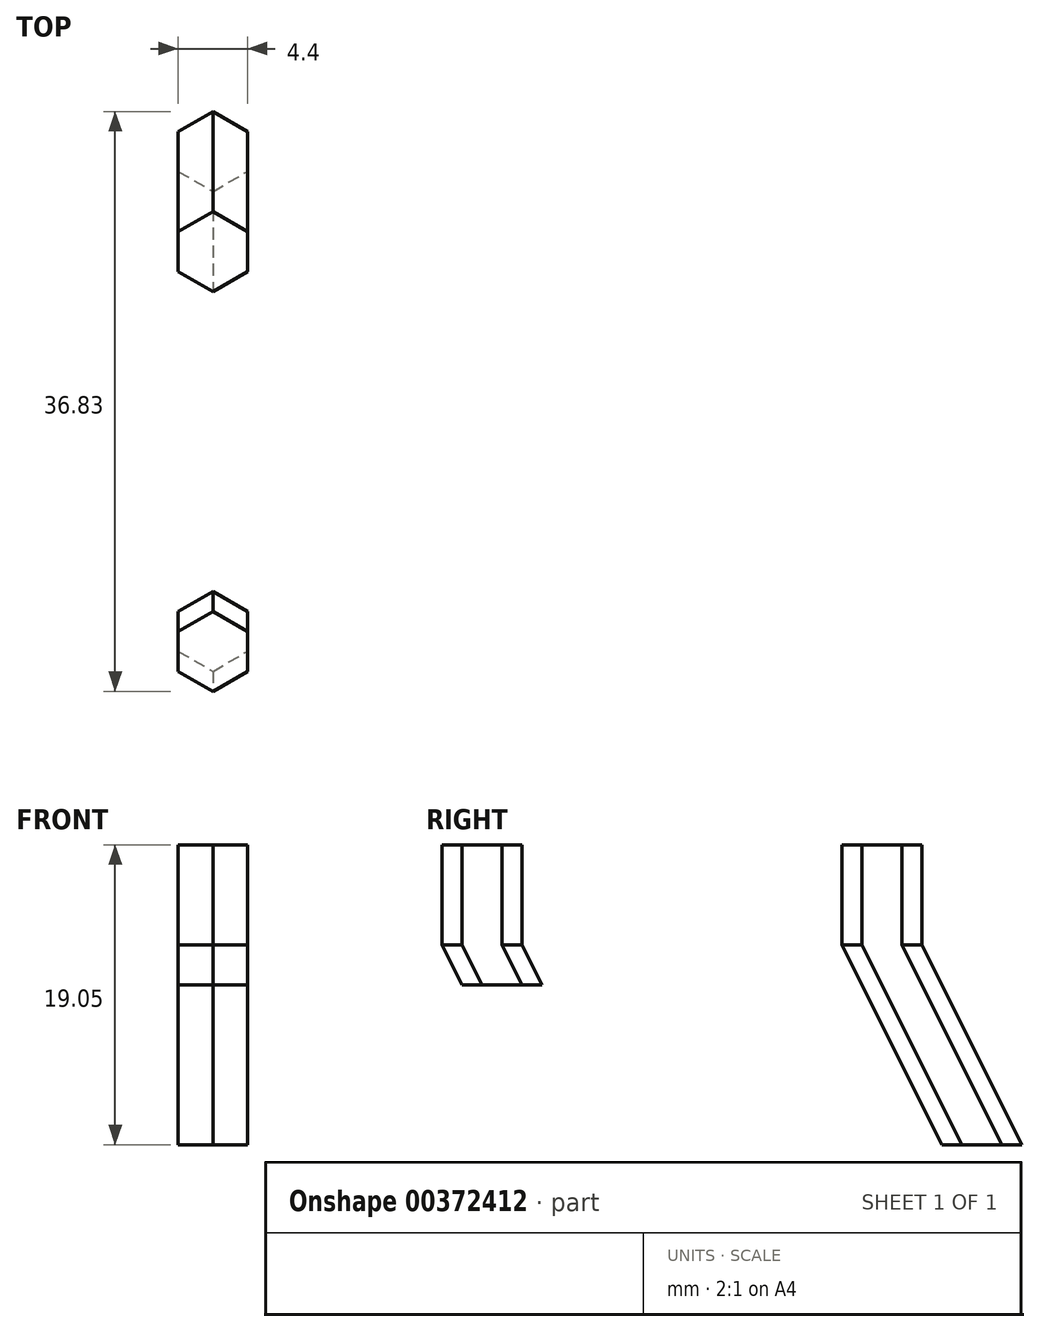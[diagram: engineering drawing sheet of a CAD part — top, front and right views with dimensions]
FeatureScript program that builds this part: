
annotation { "Feature Type Name" : "Feature", "Feature Type Description" : "" }
export const myFeature = defineFeature(function(context is Context, id is Id, definition is map)
    precondition{}
    {
        {
            var Q0;
            Q0=qCreatedBy(makeId("Top.planeOp"),FACE);
            var sketch = newSketch(context, id + "F0", { "sketchPlane" : qUnion([Q0])});
            skLineSegment(sketch, "E0.bottom", {"start": v(12.7, 12.7) * mm, "end": v(-12.7, 12.7) * mm});
            skLineSegment(sketch, "E0.top", {"start": v(12.7, -12.7) * mm, "end": v(-12.7, -12.7) * mm});
            skLineSegment(sketch, "E0.left", {"start": v(12.7, 12.7) * mm, "end": v(12.7, -12.7) * mm});
            skLineSegment(sketch, "E0.right", {"start": v(-12.7, 12.7) * mm, "end": v(-12.7, -12.7) * mm});
            skPoint(sketch, "E0.middle", {"position": v(0, 0) * mm});
            skCircle(sketch, "E1", {"center": v(12.7, 12.7) * mm, "radius": 2.54 * mm});
            skCircle(sketch, "E2", {"center": v(12.7, -12.7) * mm, "radius": 2.54 * mm});
            skCircle(sketch, "E3.cCircle", {"center": v(12.7, 12.7) * mm, "radius": 2.54 * mm, "construction": true});
            skLineSegment(sketch, "E3.0", {"start": v(12.7, 15.24) * mm, "end": v(14.9, 13.97) * mm});
            skLineSegment(sketch, "E3.1", {"start": v(14.9, 13.97) * mm, "end": v(14.9, 11.43) * mm});
            skLineSegment(sketch, "E3.2", {"start": v(14.9, 11.43) * mm, "end": v(12.7, 10.16) * mm});
            skLineSegment(sketch, "E3.3", {"start": v(12.7, 10.16) * mm, "end": v(10.5, 11.43) * mm});
            skLineSegment(sketch, "E3.4", {"start": v(10.5, 11.43) * mm, "end": v(10.5, 13.97) * mm});
            skLineSegment(sketch, "E3.5", {"start": v(10.5, 13.97) * mm, "end": v(12.7, 15.24) * mm});
            skCircle(sketch, "E4.cCircle", {"center": v(12.7, -12.7) * mm, "radius": 2.54 * mm, "construction": true});
            skLineSegment(sketch, "E4.0", {"start": v(12.7, -10.16) * mm, "end": v(14.9, -11.43) * mm});
            skLineSegment(sketch, "E4.1", {"start": v(14.9, -11.43) * mm, "end": v(14.9, -13.97) * mm});
            skLineSegment(sketch, "E4.2", {"start": v(14.9, -13.97) * mm, "end": v(12.7, -15.24) * mm});
            skLineSegment(sketch, "E4.3", {"start": v(12.7, -15.24) * mm, "end": v(10.5, -13.97) * mm});
            skLineSegment(sketch, "E4.4", {"start": v(10.5, -13.97) * mm, "end": v(10.5, -11.43) * mm});
            skLineSegment(sketch, "E4.5", {"start": v(10.5, -11.43) * mm, "end": v(12.7, -10.16) * mm});
            skSolve(sketch);
        }
        {
            var Q0;
            Q0=makeQuery(id+"F0.imprint","IMPRINT",FACE,{"disambiguationData":[TD([[makeQuery(id+"F0.imprint","IMPRINT",EDGE,{"derivedFrom":sQuery(id+"F0.wireOp",EDGE,"E3.0")}),-1.0]])]});
            var Q1;
            {var subQ5=sQuery(id+"F0.wireOp",EDGE,"E3.3");Q1=makeQuery(id+"F0.imprint","IMPRINT",FACE,{"disambiguationData":[TD([[makeQuery(id+"F0.imprint","IMPRINT",EDGE,{"derivedFrom":subQ5}),-1.0]])]});}
            var Q2;
            {var subQ5=sQuery(id+"F0.wireOp",EDGE,"E4.5");Q2=makeQuery(id+"F0.imprint","IMPRINT",FACE,{"disambiguationData":[TD([[makeQuery(id+"F0.imprint","IMPRINT",EDGE,{"derivedFrom":subQ5}),-1.0]])]});}
            var Q3;
            {var subQ0=sQuery(id+"F0.wireOp",EDGE,"E4.0");Q3=makeQuery(id+"F0.imprint","IMPRINT",FACE,{"disambiguationData":[TD([[makeQuery(id+"F0.imprint","IMPRINT",EDGE,{"derivedFrom":subQ0}),-1.0]])]});}
            extrude(context, id + "F1", {"entities" : qUnion([Q0, Q1, Q2, Q3]), "oppositeDirection" : true, "depth" : 6.35 * mm, "offsetDistance" : 25.4 * mm});
        }
        {
            var Q0;
            Q0=makeQuery(id+"F1.opExtrude","CAP_FACE",FACE,{"disambiguationData":[OSD([sQuery(id+"F0.wireOp",EDGE,"E4.0"),sQuery(id+"F0.wireOp",EDGE,"E4.1"),sQuery(id+"F0.wireOp",EDGE,"E4.2"),sQuery(id+"F0.wireOp",EDGE,"E4.3"),sQuery(id+"F0.wireOp",EDGE,"E4.4"),sQuery(id+"F0.wireOp",EDGE,"E4.5")])],"isStart":false});
            cPlane(context, id + "F2", {"entities" : qUnion([Q0]), "cplaneType" : CPlaneType.OFFSET, "offset" : 2.54 * mm, "width" : 152.4 * mm, "height" : 152.4 * mm});
        }
        {
            var Q0;
            Q0=qCreatedBy(id+"F2.planeOp",FACE);
            var sketch = newSketch(context, id + "F3", { "sketchPlane" : qUnion([Q0])});
            skPoint(sketch, "E5.0", {"position": v(12.7, 10.16) * mm});
            skLineSegment(sketch, "E6", {"start": v(12.7, 10.16) * mm, "end": v(12.7, 8.9) * mm, "construction": true});
            skLineSegment(sketch, "E7.0", {"start": v(12.7, 10.16) * mm, "end": v(14.9, 11.43) * mm, "construction": true});
            skLineSegment(sketch, "E8.0", {"start": v(14.9, 11.43) * mm, "end": v(14.9, 13.97) * mm, "construction": true});
            skLineSegment(sketch, "E9.0", {"start": v(14.9, 13.97) * mm, "end": v(12.7, 15.24) * mm, "construction": true});
            skLineSegment(sketch, "E10.0", {"start": v(12.7, 15.24) * mm, "end": v(10.5, 13.97) * mm, "construction": true});
            skLineSegment(sketch, "E11.0", {"start": v(10.5, 13.97) * mm, "end": v(10.5, 11.43) * mm, "construction": true});
            skLineSegment(sketch, "E12.0", {"start": v(10.5, 11.43) * mm, "end": v(12.7, 10.16) * mm, "construction": true});
            skLineSegment(sketch, "E13", {"start": v(14.9, 11.43) * mm, "end": v(10.5, 13.97) * mm, "construction": true});
            skLineSegment(sketch, "E14", {"start": v(12.7, 12.7) * mm, "end": v(12.7, 11.43) * mm, "construction": true});
            skCircle(sketch, "E15.cCircle", {"center": v(12.7, 11.43) * mm, "radius": 2.54 * mm, "construction": true});
            skLineSegment(sketch, "E15.0", {"start": v(12.7, 8.9) * mm, "end": v(10.5, 10.16) * mm});
            skLineSegment(sketch, "E15.1", {"start": v(10.5, 10.16) * mm, "end": v(10.5, 12.7) * mm});
            skLineSegment(sketch, "E15.2", {"start": v(10.5, 12.7) * mm, "end": v(12.7, 13.97) * mm});
            skLineSegment(sketch, "E15.3", {"start": v(12.7, 13.97) * mm, "end": v(14.9, 12.7) * mm});
            skLineSegment(sketch, "E15.4", {"start": v(14.9, 12.7) * mm, "end": v(14.9, 10.16) * mm});
            skLineSegment(sketch, "E15.5", {"start": v(14.9, 10.16) * mm, "end": v(12.7, 8.9) * mm});
            skSolve(sketch);
        }
        {
            var Q1;
            Q1=makeQuery(id+"F3.imprint","IMPRINT",FACE,{"disambiguationData":[TD([[makeQuery(id+"F3.imprint","IMPRINT",EDGE,{"derivedFrom":sQuery(id+"F3.wireOp",EDGE,"E15.0")}),-1.0]])]});
            var Q2;
            Q2=makeQuery(id+"F1.opExtrude","CAP_FACE",FACE,{"disambiguationData":[OSD([sQuery(id+"F0.wireOp",EDGE,"E4.0"),sQuery(id+"F0.wireOp",EDGE,"E4.1"),sQuery(id+"F0.wireOp",EDGE,"E4.2"),sQuery(id+"F0.wireOp",EDGE,"E4.3"),sQuery(id+"F0.wireOp",EDGE,"E4.4"),sQuery(id+"F0.wireOp",EDGE,"E4.5")])],"isStart":false});
            loft(context, id + "F4", {"operationType" : NewBodyOperationType.ADD, "sheetProfilesArray" : [{ "sheetProfileEntities" : qUnion([Q1]) }, { "sheetProfileEntities" : qUnion([Q2]) }]});
        }
        {
            var Q0;
            Q0=makeQuery(id+"F1.opExtrude","CAP_FACE",FACE,{"disambiguationData":[OSD([sQuery(id+"F0.wireOp",EDGE,"E3.0"),sQuery(id+"F0.wireOp",EDGE,"E3.1"),sQuery(id+"F0.wireOp",EDGE,"E3.2"),sQuery(id+"F0.wireOp",EDGE,"E3.3"),sQuery(id+"F0.wireOp",EDGE,"E3.4"),sQuery(id+"F0.wireOp",EDGE,"E3.5")])],"isStart":false});
            cPlane(context, id + "F5", {"entities" : qUnion([Q0]), "cplaneType" : CPlaneType.OFFSET, "offset" : 12.7 * mm, "width" : 152.4 * mm, "height" : 152.4 * mm});
        }
        {
            var Q0;
            Q0=qCreatedBy(id+"F5.planeOp",FACE);
            var sketch = newSketch(context, id + "F6", { "sketchPlane" : qUnion([Q0])});
            skPoint(sketch, "E16.0", {"position": v(12.7, -15.24) * mm});
            skPoint(sketch, "E17.0", {"position": v(10.5, -11.43) * mm});
            skPoint(sketch, "E18.0", {"position": v(14.9, -13.97) * mm});
            skLineSegment(sketch, "E19", {"start": v(10.5, -11.43) * mm, "end": v(14.9, -13.97) * mm, "construction": true});
            skLineSegment(sketch, "E20", {"start": v(12.7, -12.7) * mm, "end": v(12.7, -19.05) * mm, "construction": true});
            skCircle(sketch, "E21.cCircle", {"center": v(12.7, -19.05) * mm, "radius": 2.54 * mm, "construction": true});
            skLineSegment(sketch, "E21.0", {"start": v(12.7, -16.5) * mm, "end": v(14.9, -17.78) * mm});
            skLineSegment(sketch, "E21.1", {"start": v(14.9, -17.78) * mm, "end": v(14.9, -20.32) * mm});
            skLineSegment(sketch, "E21.2", {"start": v(14.9, -20.32) * mm, "end": v(12.7, -21.59) * mm});
            skLineSegment(sketch, "E21.3", {"start": v(12.7, -21.59) * mm, "end": v(10.5, -20.32) * mm});
            skLineSegment(sketch, "E21.4", {"start": v(10.5, -20.32) * mm, "end": v(10.5, -17.78) * mm});
            skLineSegment(sketch, "E21.5", {"start": v(10.5, -17.78) * mm, "end": v(12.7, -16.5) * mm});
            skSolve(sketch);
        }
        {
            var Q1;
            Q1=makeQuery(id+"F6.imprint","IMPRINT",FACE,{"disambiguationData":[TD([[makeQuery(id+"F6.imprint","IMPRINT",EDGE,{"derivedFrom":sQuery(id+"F6.wireOp",EDGE,"E21.0")}),-1.0]])]});
            var Q2;
            Q2=makeQuery(id+"F1.opExtrude","CAP_FACE",FACE,{"disambiguationData":[OSD([sQuery(id+"F0.wireOp",EDGE,"E3.0"),sQuery(id+"F0.wireOp",EDGE,"E3.1"),sQuery(id+"F0.wireOp",EDGE,"E3.2"),sQuery(id+"F0.wireOp",EDGE,"E3.3"),sQuery(id+"F0.wireOp",EDGE,"E3.4"),sQuery(id+"F0.wireOp",EDGE,"E3.5")])],"isStart":false});
            loft(context, id + "F7", {"operationType" : NewBodyOperationType.ADD, "sheetProfilesArray" : [{ "sheetProfileEntities" : qUnion([Q1]) }, { "sheetProfileEntities" : qUnion([Q2]) }]});
        }
    });
